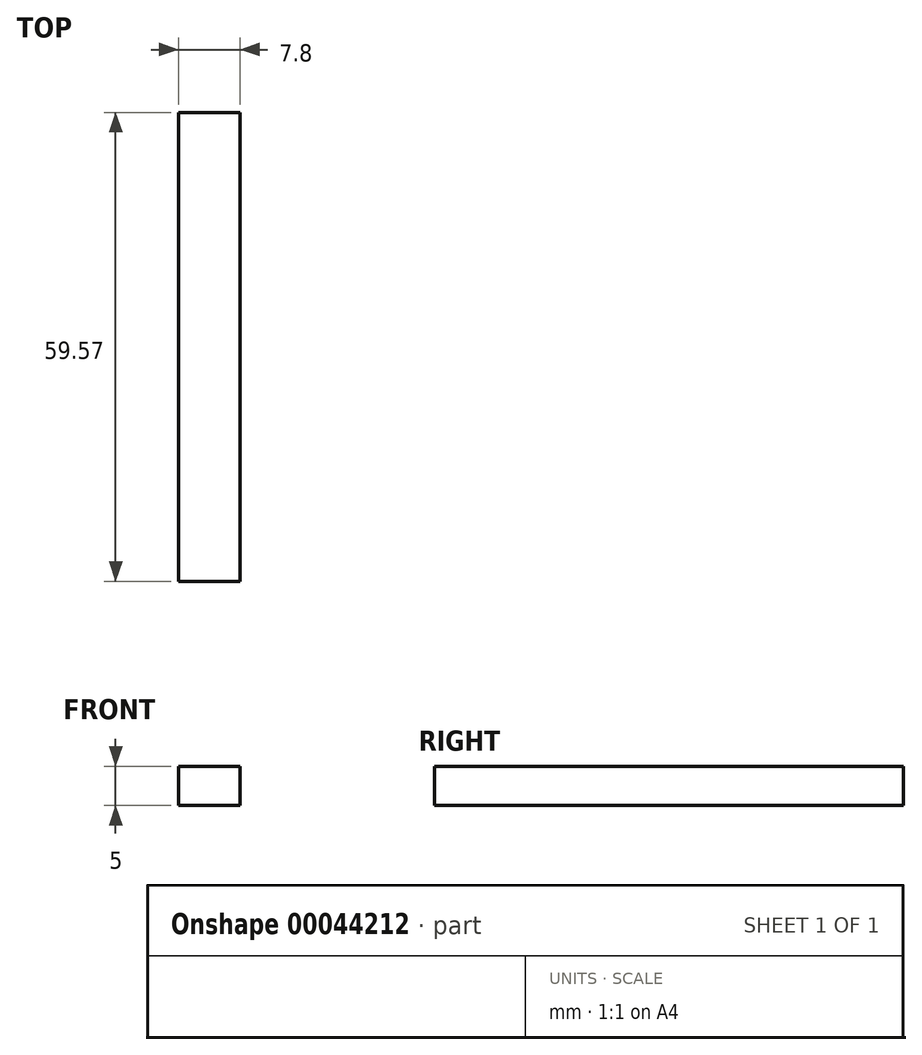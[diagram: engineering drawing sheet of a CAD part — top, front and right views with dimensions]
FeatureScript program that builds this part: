
annotation { "Feature Type Name" : "Feature", "Feature Type Description" : "" }
export const myFeature = defineFeature(function(context is Context, id is Id, definition is map)
    precondition{}
    {
        {
            var Q0;
            Q0=qCreatedBy(makeId("Top.planeOp"),FACE);
            var sketch = newSketch(context, id + "F0", { "sketchPlane" : qUnion([Q0])});
            skLineSegment(sketch, "E0.bottom", {"start": v(0, 0) * mm, "end": v(-7.8, 0) * mm});
            skLineSegment(sketch, "E0.top", {"start": v(0, 59.57) * mm, "end": v(-7.8, 59.57) * mm});
            skLineSegment(sketch, "E0.left", {"start": v(0, 0) * mm, "end": v(0, 59.57) * mm});
            skLineSegment(sketch, "E0.right", {"start": v(-7.8, 0) * mm, "end": v(-7.8, 59.57) * mm});
            skSolve(sketch);
        }
        {
            var Q0;
            Q0=makeQuery(id+"F0.imprint","IMPRINT",FACE,{"disambiguationData":[TD([[makeQuery(id+"F0.imprint","IMPRINT",EDGE,{"derivedFrom":sQuery(id+"F0.wireOp",EDGE,"E0.bottom")}),-1.0]])]});
            extrude(context, id + "F1", {"entities" : qUnion([Q0]), "depth" : 5 * mm});
        }
    });
